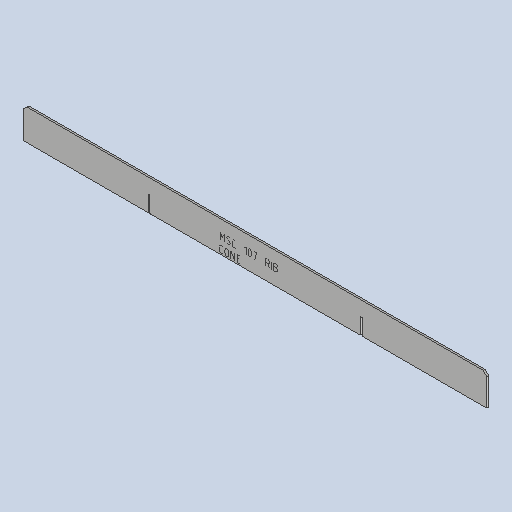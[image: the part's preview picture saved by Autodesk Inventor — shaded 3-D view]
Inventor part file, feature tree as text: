
AUTODESK INVENTOR PART (.ipt)
format: ipt  version: 2025 (Build 290162010, 162A)  size: 371,200 bytes
history: native  units: mm
features: other x5, sketch x3, sheet_metal_op x1, extrude x1
ambient origin geometry x8: Origin, YZ Plane, XZ Plane, XY Plane, X Axis, Y Axis, Z Axis, Center Point
bodies: Body1 (feature_tree)
feature tree (10):
  sheet_metal_op  "Face1"
  extrude  "Extrusion1"  Depth=50.0mm
  other  "Mark1"
  other  "A-Side Definition"
  other  "Corner Chamfer2"
  sketch  "Sketch2"  dims[d18=750.0mm d19=50.0mm]
  other  "Plate2"
  sketch  "Sketch3"  dims[d20=45.0mm]
  sketch  "Sketch5"  dims[d21=3.0mm d24=26.0mm d25=0.0mm d26=0.0mm d44=3.1mm d45=340.0mm d46=6.0mm d47=6.0mm d48=45.0deg]
  other  "Definition1"
